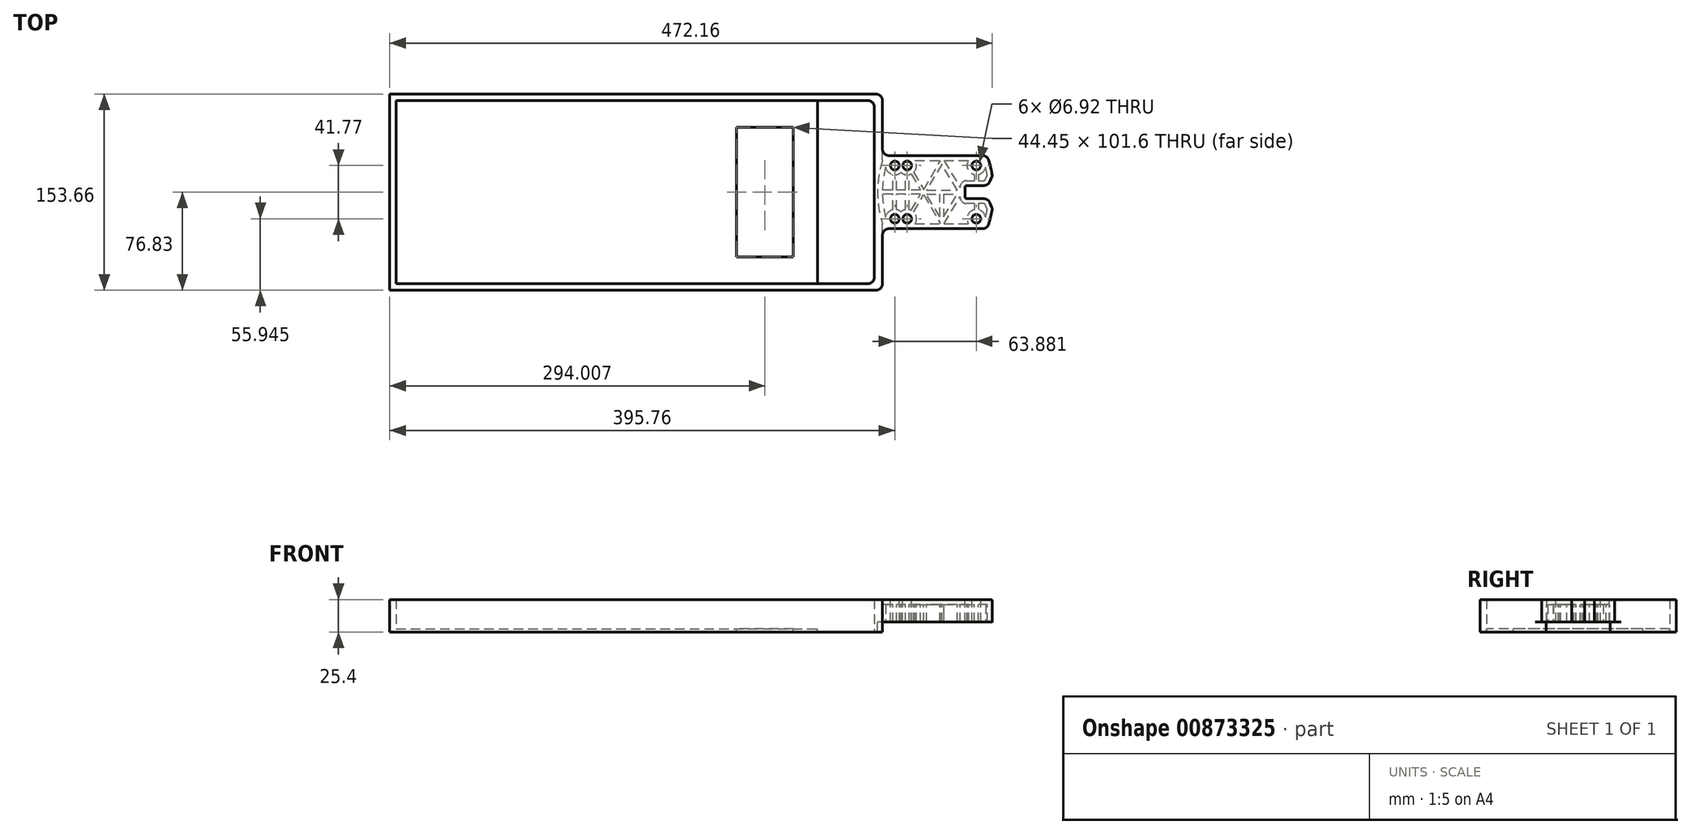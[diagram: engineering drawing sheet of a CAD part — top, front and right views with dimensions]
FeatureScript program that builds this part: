
annotation { "Feature Type Name" : "Feature", "Feature Type Description" : "" }
export const myFeature = defineFeature(function(context is Context, id is Id, definition is map)
    precondition{}
    {
        {
            var Q0;
            Q0=qCreatedBy(makeId("Top.planeOp"),FACE);
            var sketch = newSketch(context, id + "F0", { "sketchPlane" : qUnion([Q0])});
            skPoint(sketch, "E0.middle", {"position": v(0, 0) * mm});
            skLineSegment(sketch, "E1", {"start": v(-45.43, 0) * mm, "end": v(45.43, 0) * mm, "construction": true});
            skLineSegment(sketch, "E2", {"start": v(0, 28.7) * mm, "end": v(0, -28.7) * mm, "construction": true});
            skLineSegment(sketch, "E3", {"start": v(-31.94, 17.42) * mm, "end": v(-31.94, -17.42) * mm, "construction": true});
            skPoint(sketch, "E4", {"position": v(-31.94, 0) * mm});
            skCircle(sketch, "E5", {"center": v(-31.94, 20.89) * mm, "radius": 3.46 * mm});
            skLineSegment(sketch, "E6", {"start": v(-22.22, -17.42) * mm, "end": v(-22.23, 17.42) * mm, "construction": true});
            skPoint(sketch, "E7", {"position": v(-22.23, 0) * mm});
            skCircle(sketch, "E8", {"center": v(-22.23, 20.89) * mm, "radius": 3.46 * mm});
            skLineSegment(sketch, "E9", {"start": v(31.94, 17.42) * mm, "end": v(31.94, -17.42) * mm, "construction": true});
            skPoint(sketch, "E10", {"position": v(31.94, 0) * mm});
            skCircle(sketch, "E11", {"center": v(31.94, 20.89) * mm, "radius": 3.46 * mm});
            skPoint(sketch, "E12", {"position": v(-28.48, 20.89) * mm});
            skPoint(sketch, "E13", {"position": v(-25.69, 20.89) * mm});
            skPoint(sketch, "E14", {"position": v(-18.76, 20.89) * mm});
            skPoint(sketch, "E15", {"position": v(28.48, 20.89) * mm});
            skLineSegment(sketch, "E16", {"start": v(-40.35, 28.7) * mm, "end": v(40.35, 28.7) * mm});
            skPoint(sketch, "E17", {"position": v(0, 28.7) * mm});
            skArc(sketch, "E18", {"start": v(-40.35, 28.7) * mm, "mid": v(-44.15, 14.57) * mm, "end": v(-45.43, 0) * mm});
            skArc(sketch, "E19", {"start": v(45.43, 0) * mm, "mid": v(44.15, 14.57) * mm, "end": v(40.35, 28.7) * mm});
            skLineSegment(sketch, "E20", {"start": v(-31.94, 20.89) * mm, "end": v(31.94, 20.89) * mm, "construction": true});
            skPoint(sketch, "E21", {"position": v(0, 20.89) * mm});
            skArc(sketch, "E22.MirrorCS", {"start": v(-40.35, -28.7) * mm, "mid": v(-44.15, -14.57) * mm, "end": v(-45.43, 0) * mm});
            skLineSegment(sketch, "E23.MirrorCS", {"start": v(-40.35, -28.7) * mm, "end": v(40.35, -28.7) * mm});
            skCircle(sketch, "E24.MirrorC", {"center": v(-31.94, -20.89) * mm, "radius": 3.46 * mm});
            skCircle(sketch, "E25.MirrorC", {"center": v(-22.23, -20.89) * mm, "radius": 3.46 * mm});
            skCircle(sketch, "E26.MirrorC", {"center": v(31.94, -20.89) * mm, "radius": 3.46 * mm});
            skArc(sketch, "E27.MirrorCS", {"start": v(45.43, 0) * mm, "mid": v(44.15, -14.57) * mm, "end": v(40.35, -28.7) * mm});
            skSolve(sketch);
        }
        {
            var Q0;
            Q0=makeQuery(id+"F0.imprint","IMPRINT",FACE,{"disambiguationData":[TD([[makeQuery(id+"F0.imprint","IMPRINT",EDGE,{"derivedFrom":sQuery(id+"F0.wireOp",EDGE,"E5")}),-1.0]])]});
            extrude(context, id + "F1", {"entities" : qUnion([Q0]), "oppositeDirection" : true, "depth" : 17.6 * mm, "offsetDistance" : 25.4 * mm});
        }
        {
            var Q0;
            Q0=makeQuery(id+"F1.opExtrude","CAP_FACE",FACE,{"disambiguationData":[OSD([sQuery(id+"F0.wireOp",EDGE,"E5"),sQuery(id+"F0.wireOp",EDGE,"E8"),sQuery(id+"F0.wireOp",EDGE,"E11"),sQuery(id+"F0.wireOp",EDGE,"E16"),sQuery(id+"F0.wireOp",EDGE,"E18"),sQuery(id+"F0.wireOp",EDGE,"E19"),sQuery(id+"F0.wireOp",EDGE,"E22.MirrorCS"),sQuery(id+"F0.wireOp",EDGE,"E23.MirrorCS"),sQuery(id+"F0.wireOp",EDGE,"E24.MirrorC"),sQuery(id+"F0.wireOp",EDGE,"E25.MirrorC"),sQuery(id+"F0.wireOp",EDGE,"E26.MirrorC"),sQuery(id+"F0.wireOp",EDGE,"E27.MirrorCS")])],"isStart":true});
            var sketch = newSketch(context, id + "F2", { "sketchPlane" : qUnion([Q0])});
            skLineSegment(sketch, "E28", {"start": v(44.46, -12.7) * mm, "end": v(41.19, -5.2) * mm});
            skLineSegment(sketch, "E29", {"start": v(41.19, -5.2) * mm, "end": v(23.15, -5.2) * mm});
            skLineSegment(sketch, "E30", {"start": v(23.15, -5.2) * mm, "end": v(23.15, 5.2) * mm});
            skLineSegment(sketch, "E31", {"start": v(23.15, 5.2) * mm, "end": v(41.19, 5.2) * mm});
            skLineSegment(sketch, "E32", {"start": v(41.19, 5.2) * mm, "end": v(44.46, 12.7) * mm});
            skPoint(sketch, "E33", {"position": v(23.15, 0) * mm});
            skLineSegment(sketch, "E34", {"start": v(44.46, -12.7) * mm, "end": v(44.46, 12.7) * mm, "construction": true});
            skPoint(sketch, "E35", {"position": v(-45.43, 0) * mm});
            skArc(sketch, "E36", {"start": v(44.46, -12.7) * mm, "mid": v(45.43, 0) * mm, "end": v(44.46, 12.7) * mm});
            skSolve(sketch);
        }
        {
            var Q0;
            Q0=makeQuery(id+"F2.imprint","IMPRINT",FACE,{"disambiguationData":[TD([[makeQuery(id+"F2.imprint","IMPRINT",EDGE,{"derivedFrom":sQuery(id+"F2.wireOp",EDGE,"E28")}),-1.0]])]});
            extrude(context, id + "F3", {"entities" : qUnion([Q0]), "operationType" : NewBodyOperationType.REMOVE, "endBound" : BoundingType.THROUGH_ALL, "oppositeDirection" : true, "depth" : 25.4 * mm, "offsetDistance" : 25.4 * mm});
        }
        {
            var Q0;
            Q0=makeQuery(id+"F1.opExtrude","SWEPT_EDGE",EDGE,{"disambiguationData":[OSD([sQuery(id+"F0.wireOp",EDGE,"E23.MirrorCS"),sQuery(id+"F0.wireOp",EDGE,"E27.MirrorCS")])]});
            var Q1;
            Q1=makeQuery(id+"F1.opExtrude","SWEPT_EDGE",EDGE,{"disambiguationData":[OSD([sQuery(id+"F0.wireOp",EDGE,"E22.MirrorCS"),sQuery(id+"F0.wireOp",EDGE,"E23.MirrorCS")])]});
            var Q2;
            Q2=makeQuery(id+"F3.boolean.opBoolean","COPY",EDGE,{"derivedFrom":makeQuery(id+"F3.opExtrude","SWEPT_EDGE",EDGE,{"disambiguationData":[OSD([sQuery(id+"F0.wireOp",EDGE,"E19"),sQuery(id+"F0.wireOp",EDGE,"E27.MirrorCS"),sQuery(id+"F2.wireOp",EDGE,"E28"),sQuery(id+"F2.wireOp",EDGE,"E36")])]})});
            var Q3;
            Q3=makeQuery(id+"F3.boolean.opBoolean","COPY",EDGE,{"derivedFrom":makeQuery(id+"F3.opExtrude","SWEPT_EDGE",EDGE,{"disambiguationData":[OSD([sQuery(id+"F2.wireOp",EDGE,"E31"),sQuery(id+"F2.wireOp",EDGE,"E32")])]})});
            var Q4;
            Q4=makeQuery(id+"F3.boolean.opBoolean","COPY",EDGE,{"derivedFrom":makeQuery(id+"F3.opExtrude","SWEPT_EDGE",EDGE,{"disambiguationData":[OSD([sQuery(id+"F0.wireOp",EDGE,"E19"),sQuery(id+"F0.wireOp",EDGE,"E27.MirrorCS"),sQuery(id+"F2.wireOp",EDGE,"E32"),sQuery(id+"F2.wireOp",EDGE,"E36")])]})});
            var Q5;
            Q5=makeQuery(id+"F1.opExtrude","SWEPT_EDGE",EDGE,{"disambiguationData":[OSD([sQuery(id+"F0.wireOp",EDGE,"E16"),sQuery(id+"F0.wireOp",EDGE,"E19")])]});
            var Q6;
            Q6=makeQuery(id+"F3.boolean.opBoolean","COPY",EDGE,{"derivedFrom":makeQuery(id+"F3.opExtrude","SWEPT_EDGE",EDGE,{"disambiguationData":[OSD([sQuery(id+"F2.wireOp",EDGE,"E28"),sQuery(id+"F2.wireOp",EDGE,"E29")])]})});
            var Q7;
            Q7=makeQuery(id+"F1.opExtrude","SWEPT_EDGE",EDGE,{"disambiguationData":[OSD([sQuery(id+"F0.wireOp",EDGE,"E16"),sQuery(id+"F0.wireOp",EDGE,"E18")])]});
            fillet(context, id + "F4", {"entities" : qUnion([Q0, Q1, Q2, Q3, Q4, Q5, Q6, Q7]), "radius" : 5.08 * mm, "tangentPropagation" : true, "allowEdgeOverflow" : false});
        }
        {
            var Q0;
            Q0=makeQuery(id+"F1.opExtrude","CAP_FACE",FACE,{"disambiguationData":[OSD([sQuery(id+"F0.wireOp",EDGE,"E5"),sQuery(id+"F0.wireOp",EDGE,"E8"),sQuery(id+"F0.wireOp",EDGE,"E11"),sQuery(id+"F0.wireOp",EDGE,"E16"),sQuery(id+"F0.wireOp",EDGE,"E18"),sQuery(id+"F0.wireOp",EDGE,"E19"),sQuery(id+"F0.wireOp",EDGE,"E22.MirrorCS"),sQuery(id+"F0.wireOp",EDGE,"E23.MirrorCS"),sQuery(id+"F0.wireOp",EDGE,"E24.MirrorC"),sQuery(id+"F0.wireOp",EDGE,"E25.MirrorC"),sQuery(id+"F0.wireOp",EDGE,"E26.MirrorC"),sQuery(id+"F0.wireOp",EDGE,"E27.MirrorCS")])],"isStart":false});
            shell(context, id + "F5", {"entities" : qUnion([Q0]), "thickness" : 3.8 * mm});
        }
        {
            var Q0;
            Q0=makeQuery(id+"F3.boolean.opBoolean","COPY",EDGE,{"derivedFrom":makeQuery(id+"F3.opExtrude","SWEPT_EDGE",EDGE,{"disambiguationData":[OSD([sQuery(id+"F2.wireOp",EDGE,"E29"),sQuery(id+"F2.wireOp",EDGE,"E30")])]})});
            var Q1;
            Q1=makeQuery(id+"F3.boolean.opBoolean","COPY",EDGE,{"derivedFrom":makeQuery(id+"F3.opExtrude","SWEPT_EDGE",EDGE,{"disambiguationData":[OSD([sQuery(id+"F2.wireOp",EDGE,"E30"),sQuery(id+"F2.wireOp",EDGE,"E31")])]})});
            fillet(context, id + "F6", {"entities" : qUnion([Q0, Q1]), "radius" : 1.27 * mm, "tangentPropagation" : true, "allowEdgeOverflow" : false});
        }
        {
            var Q0;
            Q0=makeQuery(id+"F5.opShell","OFFSET_EDGE",EDGE,{"disambiguationData":[OSD([sQuery(id+"F2.wireOp",EDGE,"E30"),sQuery(id+"F2.wireOp",EDGE,"E31")])]});
            var Q1;
            Q1=makeQuery(id+"F5.opShell","OFFSET_EDGE",EDGE,{"disambiguationData":[OSD([sQuery(id+"F2.wireOp",EDGE,"E29"),sQuery(id+"F2.wireOp",EDGE,"E30")])]});
            fillet(context, id + "F7", {"entities" : qUnion([Q0, Q1]), "radius" : 5.08 * mm, "tangentPropagation" : true, "allowEdgeOverflow" : false});
        }
        {
            var Q0;
            Q0=makeQuery(id+"F5.opShell","OFFSET_FACE",FACE,{"disambiguationData":[OSD([sQuery(id+"F0.wireOp",EDGE,"E5"),sQuery(id+"F0.wireOp",EDGE,"E8"),sQuery(id+"F0.wireOp",EDGE,"E11"),sQuery(id+"F0.wireOp",EDGE,"E16"),sQuery(id+"F0.wireOp",EDGE,"E18"),sQuery(id+"F0.wireOp",EDGE,"E19"),sQuery(id+"F0.wireOp",EDGE,"E22.MirrorCS"),sQuery(id+"F0.wireOp",EDGE,"E23.MirrorCS"),sQuery(id+"F0.wireOp",EDGE,"E24.MirrorC"),sQuery(id+"F0.wireOp",EDGE,"E25.MirrorC"),sQuery(id+"F0.wireOp",EDGE,"E26.MirrorC"),sQuery(id+"F0.wireOp",EDGE,"E27.MirrorCS")])]});
            var sketch = newSketch(context, id + "F8", { "sketchPlane" : qUnion([Q0])});
            skLineSegment(sketch, "E37", {"start": v(-31.94, 20.89) * mm, "end": v(-31.94, -20.89) * mm, "construction": true});
            skLineSegment(sketch, "E38", {"start": v(-22.23, -20.89) * mm, "end": v(-22.23, 20.89) * mm, "construction": true});
            skLineSegment(sketch, "E39", {"start": v(31.94, -20.89) * mm, "end": v(31.94, 20.89) * mm, "construction": true});
            skLineSegment(sketch, "E40.bottom", {"start": v(-33.44, 13.77) * mm, "end": v(-30.44, 13.77) * mm});
            skLineSegment(sketch, "E40.top", {"start": v(-33.44, -13.77) * mm, "end": v(-30.44, -13.77) * mm});
            skLineSegment(sketch, "E40.left", {"start": v(-33.44, 13.77) * mm, "end": v(-33.44, 1.5) * mm});
            skLineSegment(sketch, "E40.right", {"start": v(-30.44, 13.77) * mm, "end": v(-30.44, 1.5) * mm});
            skPoint(sketch, "E40.middle", {"position": v(-31.94, 0) * mm});
            skLineSegment(sketch, "E41.bottom", {"start": v(-23.73, 13.77) * mm, "end": v(-20.73, 13.77) * mm});
            skLineSegment(sketch, "E41.top", {"start": v(-23.73, -13.77) * mm, "end": v(-20.73, -13.77) * mm});
            skLineSegment(sketch, "E41.left", {"start": v(-23.73, 13.77) * mm, "end": v(-23.73, 1.5) * mm});
            skLineSegment(sketch, "E41.right", {"start": v(-20.73, 13.77) * mm, "end": v(-20.73, 1.5) * mm});
            skPoint(sketch, "E41.middle", {"position": v(-22.23, 0) * mm});
            skLineSegment(sketch, "E42.bottom", {"start": v(33.44, -13.77) * mm, "end": v(30.44, -13.77) * mm});
            skLineSegment(sketch, "E42.top", {"start": v(33.44, -9.02) * mm, "end": v(30.44, -9.02) * mm});
            skLineSegment(sketch, "E42.left", {"start": v(33.44, -13.77) * mm, "end": v(33.44, -9.02) * mm});
            skLineSegment(sketch, "E42.right", {"start": v(30.44, -13.77) * mm, "end": v(30.44, -9.02) * mm});
            skPoint(sketch, "E42.middle", {"position": v(31.94, -11.4) * mm});
            skLineSegment(sketch, "E43.bottom", {"start": v(33.44, 9.02) * mm, "end": v(30.44, 9.02) * mm});
            skLineSegment(sketch, "E43.top", {"start": v(33.44, 13.77) * mm, "end": v(30.44, 13.77) * mm});
            skLineSegment(sketch, "E43.left", {"start": v(33.44, 9.02) * mm, "end": v(33.44, 13.77) * mm});
            skLineSegment(sketch, "E43.right", {"start": v(30.44, 9.02) * mm, "end": v(30.44, 13.77) * mm});
            skPoint(sketch, "E43.middle", {"position": v(31.94, 11.4) * mm});
            skLineSegment(sketch, "E44.right", {"start": v(-45.41, -1.5) * mm, "end": v(-45.41, 1.5) * mm});
            skPoint(sketch, "E44.middle", {"position": v(-13.04, 0) * mm});
            skLineSegment(sketch, "E45", {"start": v(-22.23, 20.89) * mm, "end": v(4.86, -24.9) * mm, "construction": true});
            skLineSegment(sketch, "E46", {"start": v(4.86, -24.9) * mm, "end": v(31.94, 20.89) * mm, "construction": true});
            skLineSegment(sketch, "E47", {"start": v(31.94, -20.89) * mm, "end": v(4.86, 24.9) * mm, "construction": true});
            skLineSegment(sketch, "E48", {"start": v(4.86, 24.9) * mm, "end": v(-22.23, -20.89) * mm, "construction": true});
            skLineSegment(sketch, "E49", {"start": v(-17.31, -15.53) * mm, "end": v(-9.27, -1.93) * mm});
            skLineSegment(sketch, "E50", {"start": v(4.86, 21.95) * mm, "end": v(16.95, 1.5) * mm});
            skLineSegment(sketch, "E51", {"start": v(-19.23, -14.26) * mm, "end": v(-11.69, -1.5) * mm});
            skLineSegment(sketch, "E52", {"start": v(6.6, 24.9) * mm, "end": v(19.34, 3.36) * mm});
            skLineSegment(sketch, "E53", {"start": v(3.93, 24.9) * mm, "end": v(6.6, 24.9) * mm});
            skArc(sketch, "E54", {"start": v(-19.23, -14.26) * mm, "mid": v(-18.22, -14.82) * mm, "end": v(-17.31, -15.53) * mm});
            skLineSegment(sketch, "E55", {"start": v(-51.7, 0) * mm, "end": v(53.56, 0) * mm, "construction": true});
            skLineSegment(sketch, "E56.MirrorCS", {"start": v(-19.23, 14.26) * mm, "end": v(-11.69, 1.5) * mm});
            skLineSegment(sketch, "E57.MirrorCS", {"start": v(-17.31, 15.53) * mm, "end": v(-9.27, 1.93) * mm});
            skLineSegment(sketch, "E58.MirrorCS", {"start": v(4.86, -21.95) * mm, "end": v(16.95, -1.5) * mm});
            skLineSegment(sketch, "E59.MirrorCS", {"start": v(6.6, -24.9) * mm, "end": v(19.34, -3.36) * mm});
            skArc(sketch, "E60.MirrorCS", {"start": v(-19.23, 14.26) * mm, "mid": v(-18.22, 14.82) * mm, "end": v(-17.31, 15.53) * mm});
            skLineSegment(sketch, "E61.trimOffspring", {"start": v(-23.73, -1.5) * mm, "end": v(-23.73, -13.77) * mm});
            skLineSegment(sketch, "E62.trimOffspring", {"start": v(-23.73, 1.5) * mm, "end": v(-30.44, 1.5) * mm});
            skLineSegment(sketch, "E63.trimOffspring", {"start": v(-20.73, -1.5) * mm, "end": v(-20.73, -13.77) * mm});
            skLineSegment(sketch, "E64.trimOffspring", {"start": v(-23.73, -1.5) * mm, "end": v(-30.44, -1.5) * mm});
            skLineSegment(sketch, "E65.trimOffspring", {"start": v(-30.44, -1.5) * mm, "end": v(-30.44, -13.77) * mm});
            skLineSegment(sketch, "E66.trimOffspring", {"start": v(-33.44, 1.5) * mm, "end": v(-45.41, 1.5) * mm});
            skLineSegment(sketch, "E67.trimOffspring", {"start": v(-33.44, -1.5) * mm, "end": v(-33.44, -13.77) * mm});
            skLineSegment(sketch, "E68.trimOffspring", {"start": v(-33.44, -1.5) * mm, "end": v(-45.41, -1.5) * mm});
            skLineSegment(sketch, "E69.trimOffspring", {"start": v(-11.69, -1.5) * mm, "end": v(-20.73, -1.5) * mm});
            skLineSegment(sketch, "E70.trimOffspring", {"start": v(-9.27, -1.93) * mm, "end": v(3.93, -24.9) * mm});
            skLineSegment(sketch, "E71.trimOffspring", {"start": v(-7.24, 1.5) * mm, "end": v(4.86, 21.95) * mm});
            skLineSegment(sketch, "E72.trimOffspring", {"start": v(-7.24, -1.5) * mm, "end": v(4.86, -21.95) * mm});
            skLineSegment(sketch, "E73.trimOffspring", {"start": v(-11.69, 1.5) * mm, "end": v(-20.73, 1.5) * mm});
            skLineSegment(sketch, "E74.trimOffspring", {"start": v(-9.27, 1.93) * mm, "end": v(3.93, 24.9) * mm});
            skLineSegment(sketch, "E75.trimOffspring", {"start": v(16.95, -1.5) * mm, "end": v(-7.24, -1.5) * mm});
            skLineSegment(sketch, "E76.trimOffspring", {"start": v(16.95, 1.5) * mm, "end": v(-7.24, 1.5) * mm});
            skLineSegment(sketch, "E77", {"start": v(19.34, -3.36) * mm, "end": v(19.34, 3.36) * mm});
            skPoint(sketch, "E78", {"position": v(19.34, 0) * mm});
            skSolve(sketch);
        }
        {
            var Q0;
            {var subQ8=sQuery(id+"F8.wireOp",EDGE,"E40.left");Q0=makeQuery(id+"F8.imprint","IMPRINT",FACE,{"disambiguationData":[TD([[makeQuery(id+"F8.imprint","IMPRINT",EDGE,{"derivedFrom":subQ8}),1.0]])]});}
            var Q1;
            Q1=makeQuery(id+"F1.opExtrude","CAP_FACE",FACE,{"disambiguationData":[OSD([sQuery(id+"F0.wireOp",EDGE,"E5"),sQuery(id+"F0.wireOp",EDGE,"E8"),sQuery(id+"F0.wireOp",EDGE,"E11"),sQuery(id+"F0.wireOp",EDGE,"E16"),sQuery(id+"F0.wireOp",EDGE,"E18"),sQuery(id+"F0.wireOp",EDGE,"E19"),sQuery(id+"F0.wireOp",EDGE,"E22.MirrorCS"),sQuery(id+"F0.wireOp",EDGE,"E23.MirrorCS"),sQuery(id+"F0.wireOp",EDGE,"E24.MirrorC"),sQuery(id+"F0.wireOp",EDGE,"E25.MirrorC"),sQuery(id+"F0.wireOp",EDGE,"E26.MirrorC"),sQuery(id+"F0.wireOp",EDGE,"E27.MirrorCS")])],"isStart":false});
            extrude(context, id + "F9", {"entities" : qUnion([Q0]), "operationType" : NewBodyOperationType.ADD, "endBound" : BoundingType.UP_TO_SURFACE, "depth" : 25.4 * mm, "endBoundEntityFace" : qUnion([Q1]), "offsetDistance" : 25.4 * mm});
        }
        {
            var Q0;
            Q0=makeQuery(id+"F8.imprint","IMPRINT",FACE,{"disambiguationData":[TD([[makeQuery(id+"F8.imprint","IMPRINT",EDGE,{"derivedFrom":sQuery(id+"F8.wireOp",EDGE,"E43.bottom")}),-1.0]])]});
            var Q1;
            Q1=makeQuery(id+"F8.imprint","IMPRINT",FACE,{"disambiguationData":[TD([[makeQuery(id+"F8.imprint","IMPRINT",EDGE,{"derivedFrom":sQuery(id+"F8.wireOp",EDGE,"E42.top")}),-1.0]])]});
            var Q2;
            {var subQ0=sQuery(id+"F0.wireOp",EDGE,"E25.MirrorC");var subQ1=sQuery(id+"F0.wireOp",EDGE,"E24.MirrorC");var subQ2=sQuery(id+"F0.wireOp",EDGE,"E22.MirrorCS");var subQ3=sQuery(id+"F0.wireOp",EDGE,"E18");var subQ4=sQuery(id+"F0.wireOp",EDGE,"E16");var subQ5=sQuery(id+"F0.wireOp",EDGE,"E8");var subQ6=sQuery(id+"F0.wireOp",EDGE,"E5");Q2=makeQuery(id+"F9.boolean.opBoolean","MERGE",FACE,{"derivedFrom":[makeQuery(id+"F1.opExtrude","CAP_FACE",FACE,{"disambiguationData":[OSD([subQ6,subQ5,sQuery(id+"F0.wireOp",EDGE,"E11"),subQ4,subQ3,sQuery(id+"F0.wireOp",EDGE,"E19"),subQ2,sQuery(id+"F0.wireOp",EDGE,"E23.MirrorCS"),subQ1,subQ0,sQuery(id+"F0.wireOp",EDGE,"E26.MirrorC"),sQuery(id+"F0.wireOp",EDGE,"E27.MirrorCS")])],"isStart":false}),makeQuery(id+"F9.opExtrude","CAP_FACE",FACE,{"disambiguationData":[OSD([subQ6,subQ5,subQ4,subQ3,subQ2,subQ1,subQ0,sQuery(id+"F8.wireOp",EDGE,"E40.left"),sQuery(id+"F8.wireOp",EDGE,"E40.right"),sQuery(id+"F8.wireOp",EDGE,"E41.left"),sQuery(id+"F8.wireOp",EDGE,"E41.right"),sQuery(id+"F8.wireOp",EDGE,"E49"),sQuery(id+"F8.wireOp",EDGE,"E50"),sQuery(id+"F8.wireOp",EDGE,"E51"),sQuery(id+"F8.wireOp",EDGE,"E52"),sQuery(id+"F8.wireOp",EDGE,"E53"),sQuery(id+"F8.wireOp",EDGE,"E54"),sQuery(id+"F8.wireOp",EDGE,"E56.MirrorCS"),sQuery(id+"F8.wireOp",EDGE,"E57.MirrorCS"),sQuery(id+"F8.wireOp",EDGE,"E58.MirrorCS"),sQuery(id+"F8.wireOp",EDGE,"E59.MirrorCS"),sQuery(id+"F8.wireOp",EDGE,"E60.MirrorCS"),sQuery(id+"F8.wireOp",EDGE,"E61.trimOffspring"),sQuery(id+"F8.wireOp",EDGE,"E62.trimOffspring"),sQuery(id+"F8.wireOp",EDGE,"E63.trimOffspring"),sQuery(id+"F8.wireOp",EDGE,"E64.trimOffspring"),sQuery(id+"F8.wireOp",EDGE,"E65.trimOffspring"),sQuery(id+"F8.wireOp",EDGE,"E66.trimOffspring"),sQuery(id+"F8.wireOp",EDGE,"E67.trimOffspring"),sQuery(id+"F8.wireOp",EDGE,"E68.trimOffspring"),sQuery(id+"F8.wireOp",EDGE,"E69.trimOffspring"),sQuery(id+"F8.wireOp",EDGE,"E70.trimOffspring"),sQuery(id+"F8.wireOp",EDGE,"E71.trimOffspring"),sQuery(id+"F8.wireOp",EDGE,"E72.trimOffspring"),sQuery(id+"F8.wireOp",EDGE,"E73.trimOffspring"),sQuery(id+"F8.wireOp",EDGE,"E74.trimOffspring"),sQuery(id+"F8.wireOp",EDGE,"E75.trimOffspring"),sQuery(id+"F8.wireOp",EDGE,"E76.trimOffspring"),sQuery(id+"F8.wireOp",EDGE,"E77")])],"isStart":false})]});}
            extrude(context, id + "F10", {"entities" : qUnion([Q0, Q1]), "operationType" : NewBodyOperationType.ADD, "endBound" : BoundingType.UP_TO_SURFACE, "depth" : 25.4 * mm, "endBoundEntityFace" : qUnion([Q2]), "offsetDistance" : 25.4 * mm});
        }
        {
            var Q0;
            Q0=makeQuery(id+"F9.boolean.opBoolean","SPLIT",FACE,{"disambiguationData":[TD([makeQuery(id+"F9.opExtrude","SWEPT_FACE",FACE,{"disambiguationData":[OSD([sQuery(id+"F8.wireOp",EDGE,"E58.MirrorCS")])]})])],"derivedFrom":makeQuery(id+"F5.opShell","OFFSET_FACE",FACE,{"disambiguationData":[OSD([sQuery(id+"F0.wireOp",EDGE,"E5"),sQuery(id+"F0.wireOp",EDGE,"E8"),sQuery(id+"F0.wireOp",EDGE,"E11"),sQuery(id+"F0.wireOp",EDGE,"E16"),sQuery(id+"F0.wireOp",EDGE,"E18"),sQuery(id+"F0.wireOp",EDGE,"E19"),sQuery(id+"F0.wireOp",EDGE,"E22.MirrorCS"),sQuery(id+"F0.wireOp",EDGE,"E23.MirrorCS"),sQuery(id+"F0.wireOp",EDGE,"E24.MirrorC"),sQuery(id+"F0.wireOp",EDGE,"E25.MirrorC"),sQuery(id+"F0.wireOp",EDGE,"E26.MirrorC"),sQuery(id+"F0.wireOp",EDGE,"E27.MirrorCS")])]})});
            var sketch = newSketch(context, id + "F11", { "sketchPlane" : qUnion([Q0])});
            skPoint(sketch, "E79", {"position": v(4.86, 0) * mm});
            skLineSegment(sketch, "E80.bottom", {"start": v(6.36, -24.9) * mm, "end": v(3.36, -24.9) * mm});
            skLineSegment(sketch, "E80.top", {"start": v(6.36, 24.9) * mm, "end": v(3.36, 24.9) * mm});
            skLineSegment(sketch, "E80.left", {"start": v(6.36, -24.9) * mm, "end": v(6.36, 24.9) * mm});
            skLineSegment(sketch, "E80.right", {"start": v(3.36, -24.9) * mm, "end": v(3.36, 24.9) * mm});
            skSolve(sketch);
        }
        {
            var Q0;
            {var subQ1=makeQuery(id+"F9.opExtrude","CAP_EDGE",EDGE,{"disambiguationData":[OSD([sQuery(id+"F8.wireOp",EDGE,"E58.MirrorCS")])],"isStart":true});var subQ3=sQuery(id+"F11.wireOp",EDGE,"E80.left");var subQ4=makeQuery(id+"F11.imprint","INTERSECT",VERTEX,{"derivedFrom":[subQ1,subQ3]});Q0=makeQuery(id+"F11.imprint","IMPRINT",FACE,{"disambiguationData":[TD([[makeQuery(id+"F11.imprint","IMPRINT",EDGE,{"disambiguationData":[TD([[subQ4,-1.0]])],"derivedFrom":subQ3}),1.0]])]});}
            var Q1;
            {var subQ0=sQuery(id+"F11.wireOp",EDGE,"E80.top");Q1=makeQuery(id+"F11.imprint","IMPRINT",FACE,{"disambiguationData":[TD([[makeQuery(id+"F11.imprint","IMPRINT",EDGE,{"derivedFrom":subQ0}),1.0]])]});}
            var Q2;
            {var subQ0=sQuery(id+"F0.wireOp",EDGE,"E26.MirrorC");var subQ1=sQuery(id+"F0.wireOp",EDGE,"E11");var subQ2=sQuery(id+"F0.wireOp",EDGE,"E25.MirrorC");var subQ3=sQuery(id+"F0.wireOp",EDGE,"E24.MirrorC");var subQ4=sQuery(id+"F0.wireOp",EDGE,"E22.MirrorCS");var subQ5=sQuery(id+"F0.wireOp",EDGE,"E18");var subQ6=sQuery(id+"F0.wireOp",EDGE,"E16");var subQ7=sQuery(id+"F0.wireOp",EDGE,"E8");var subQ8=sQuery(id+"F0.wireOp",EDGE,"E5");Q2=makeQuery(id+"F10.boolean.opBoolean","MERGE",FACE,{"derivedFrom":[makeQuery(id+"F9.boolean.opBoolean","MERGE",FACE,{"derivedFrom":[makeQuery(id+"F1.opExtrude","CAP_FACE",FACE,{"disambiguationData":[OSD([subQ8,subQ7,subQ1,subQ6,subQ5,sQuery(id+"F0.wireOp",EDGE,"E19"),subQ4,sQuery(id+"F0.wireOp",EDGE,"E23.MirrorCS"),subQ3,subQ2,subQ0,sQuery(id+"F0.wireOp",EDGE,"E27.MirrorCS")])],"isStart":false}),makeQuery(id+"F9.opExtrude","CAP_FACE",FACE,{"disambiguationData":[OSD([subQ8,subQ7,subQ6,subQ5,subQ4,subQ3,subQ2,sQuery(id+"F8.wireOp",EDGE,"E40.left"),sQuery(id+"F8.wireOp",EDGE,"E40.right"),sQuery(id+"F8.wireOp",EDGE,"E41.left"),sQuery(id+"F8.wireOp",EDGE,"E41.right"),sQuery(id+"F8.wireOp",EDGE,"E49"),sQuery(id+"F8.wireOp",EDGE,"E50"),sQuery(id+"F8.wireOp",EDGE,"E51"),sQuery(id+"F8.wireOp",EDGE,"E52"),sQuery(id+"F8.wireOp",EDGE,"E53"),sQuery(id+"F8.wireOp",EDGE,"E54"),sQuery(id+"F8.wireOp",EDGE,"E56.MirrorCS"),sQuery(id+"F8.wireOp",EDGE,"E57.MirrorCS"),sQuery(id+"F8.wireOp",EDGE,"E58.MirrorCS"),sQuery(id+"F8.wireOp",EDGE,"E59.MirrorCS"),sQuery(id+"F8.wireOp",EDGE,"E60.MirrorCS"),sQuery(id+"F8.wireOp",EDGE,"E61.trimOffspring"),sQuery(id+"F8.wireOp",EDGE,"E62.trimOffspring"),sQuery(id+"F8.wireOp",EDGE,"E63.trimOffspring"),sQuery(id+"F8.wireOp",EDGE,"E64.trimOffspring"),sQuery(id+"F8.wireOp",EDGE,"E65.trimOffspring"),sQuery(id+"F8.wireOp",EDGE,"E66.trimOffspring"),sQuery(id+"F8.wireOp",EDGE,"E67.trimOffspring"),sQuery(id+"F8.wireOp",EDGE,"E68.trimOffspring"),sQuery(id+"F8.wireOp",EDGE,"E69.trimOffspring"),sQuery(id+"F8.wireOp",EDGE,"E70.trimOffspring"),sQuery(id+"F8.wireOp",EDGE,"E71.trimOffspring"),sQuery(id+"F8.wireOp",EDGE,"E72.trimOffspring"),sQuery(id+"F8.wireOp",EDGE,"E73.trimOffspring"),sQuery(id+"F8.wireOp",EDGE,"E74.trimOffspring"),sQuery(id+"F8.wireOp",EDGE,"E75.trimOffspring"),sQuery(id+"F8.wireOp",EDGE,"E76.trimOffspring"),sQuery(id+"F8.wireOp",EDGE,"E77")])],"isStart":false})]}),makeQuery(id+"F10.opExtrude","CAP_FACE",FACE,{"disambiguationData":[OSD([subQ1,sQuery(id+"F8.wireOp",EDGE,"E42.top"),sQuery(id+"F8.wireOp",EDGE,"E42.left"),sQuery(id+"F8.wireOp",EDGE,"E42.right")])],"isStart":false}),makeQuery(id+"F10.opExtrude","CAP_FACE",FACE,{"disambiguationData":[OSD([subQ0,sQuery(id+"F8.wireOp",EDGE,"E43.bottom"),sQuery(id+"F8.wireOp",EDGE,"E43.left"),sQuery(id+"F8.wireOp",EDGE,"E43.right")])],"isStart":false})]});}
            extrude(context, id + "F12", {"entities" : qUnion([Q0, Q1]), "operationType" : NewBodyOperationType.ADD, "endBound" : BoundingType.UP_TO_SURFACE, "depth" : 25.4 * mm, "endBoundEntityFace" : qUnion([Q2]), "offsetDistance" : 25.4 * mm});
        }
        {
            var Q0;
            Q0=qCreatedBy(makeId("Top.planeOp"),FACE);
            var sketch = newSketch(context, id + "F13", { "sketchPlane" : qUnion([Q0])});
            skLineSegment(sketch, "E81.bottom", {"start": v(-41.56, -76.83) * mm, "end": v(-427.7, -76.83) * mm});
            skLineSegment(sketch, "E81.top", {"start": v(-41.56, 76.83) * mm, "end": v(-427.7, 76.83) * mm});
            skLineSegment(sketch, "E81.left", {"start": v(-41.56, -76.83) * mm, "end": v(-41.56, -33.55) * mm});
            skLineSegment(sketch, "E81.right", {"start": v(-427.7, -76.83) * mm, "end": v(-427.7, 76.83) * mm});
            skPoint(sketch, "E81.middle", {"position": v(-234.63, 0) * mm});
            skArc(sketch, "E82", {"start": v(-36.71, -28.7) * mm, "mid": v(-40.14, -30.12) * mm, "end": v(-41.56, -33.55) * mm});
            skArc(sketch, "E83", {"start": v(-41.56, 33.55) * mm, "mid": v(-40.14, 30.12) * mm, "end": v(-36.71, 28.7) * mm});
            skLineSegment(sketch, "E84.trimOffspring", {"start": v(-41.56, 33.55) * mm, "end": v(-41.56, 76.83) * mm});
            skArc(sketch, "E85.0", {"start": v(-41.56, 25.15) * mm, "mid": v(-39.72, 27.72) * mm, "end": v(-36.71, 28.7) * mm});
            skArc(sketch, "E86.0", {"start": v(-41.56, 25.15) * mm, "mid": v(-45.43, 0) * mm, "end": v(-41.56, -25.15) * mm});
            skArc(sketch, "E87.0", {"start": v(-36.71, -28.7) * mm, "mid": v(-39.72, -27.72) * mm, "end": v(-41.56, -25.15) * mm});
            skLineSegment(sketch, "E88.bottom", {"start": v(-422.62, -71.75) * mm, "end": v(-47.97, -71.75) * mm, "construction": true});
            skLineSegment(sketch, "E88.top", {"start": v(-422.62, 71.76) * mm, "end": v(-47.97, 71.76) * mm, "construction": true});
            skLineSegment(sketch, "E88.left", {"start": v(-422.62, -71.75) * mm, "end": v(-422.62, 71.76) * mm, "construction": true});
            skLineSegment(sketch, "E88.right", {"start": v(-47.97, -71.75) * mm, "end": v(-47.97, 71.76) * mm, "construction": true});
            skPoint(sketch, "E88.middle", {"position": v(-235.3, 0) * mm});
            skLineSegment(sketch, "E89", {"start": v(-92.42, -71.75) * mm, "end": v(-92.42, 71.76) * mm, "construction": true});
            skPoint(sketch, "E90", {"position": v(-45.43, 0) * mm});
            skSolve(sketch);
        }
        {
            var Q0;
            Q0=makeQuery(id+"F13.imprint","IMPRINT",FACE,{"disambiguationData":[TD([[makeQuery(id+"F13.imprint","IMPRINT",EDGE,{"derivedFrom":sQuery(id+"F13.wireOp",EDGE,"E81.bottom")}),-1.0]])]});
            extrude(context, id + "F14", {"entities" : qUnion([Q0]), "oppositeDirection" : true, "depth" : 25.4 * mm, "offsetDistance" : 25.4 * mm});
        }
        {
            var Q0;
            Q0=makeQuery(id+"F14.opExtrude","SWEPT_BODY",BODY,{"disambiguationData":[OSD([sQuery(id+"F13.wireOp",EDGE,"E81.bottom"),sQuery(id+"F13.wireOp",EDGE,"E81.top"),sQuery(id+"F13.wireOp",EDGE,"E81.left"),sQuery(id+"F13.wireOp",EDGE,"E81.right"),sQuery(id+"F13.wireOp",EDGE,"E82"),sQuery(id+"F13.wireOp",EDGE,"E83"),sQuery(id+"F13.wireOp",EDGE,"E84.trimOffspring"),sQuery(id+"F13.wireOp",EDGE,"E85.0"),sQuery(id+"F13.wireOp",EDGE,"E86.0"),sQuery(id+"F13.wireOp",EDGE,"E87.0")])]});
            var Q1;
            Q1=makeQuery(id+"F1.opExtrude","SWEPT_BODY",BODY,{"disambiguationData":[OSD([sQuery(id+"F0.wireOp",EDGE,"E5"),sQuery(id+"F0.wireOp",EDGE,"E8"),sQuery(id+"F0.wireOp",EDGE,"E11"),sQuery(id+"F0.wireOp",EDGE,"E16"),sQuery(id+"F0.wireOp",EDGE,"E18"),sQuery(id+"F0.wireOp",EDGE,"E19"),sQuery(id+"F0.wireOp",EDGE,"E22.MirrorCS"),sQuery(id+"F0.wireOp",EDGE,"E23.MirrorCS"),sQuery(id+"F0.wireOp",EDGE,"E24.MirrorC"),sQuery(id+"F0.wireOp",EDGE,"E25.MirrorC"),sQuery(id+"F0.wireOp",EDGE,"E26.MirrorC"),sQuery(id+"F0.wireOp",EDGE,"E27.MirrorCS")])]});
            booleanBodies(context, id + "F15", {"operationType" : BooleanOperationType.UNION, "tools" : qUnion([Q0, Q1])});
        }
        {
            var Q0;
            {var subQ0=sQuery(id+"F8.wireOp",EDGE,"E72.trimOffspring");var subQ1=sQuery(id+"F8.wireOp",EDGE,"E58.MirrorCS");var subQ2=sQuery(id+"F0.wireOp",EDGE,"E26.MirrorC");var subQ3=sQuery(id+"F0.wireOp",EDGE,"E11");var subQ4=sQuery(id+"F0.wireOp",EDGE,"E25.MirrorC");var subQ5=sQuery(id+"F0.wireOp",EDGE,"E24.MirrorC");var subQ6=sQuery(id+"F0.wireOp",EDGE,"E22.MirrorCS");var subQ7=sQuery(id+"F0.wireOp",EDGE,"E18");var subQ8=sQuery(id+"F0.wireOp",EDGE,"E16");var subQ9=sQuery(id+"F0.wireOp",EDGE,"E8");var subQ10=sQuery(id+"F0.wireOp",EDGE,"E5");Q0=makeQuery(id+"F12.boolean.opBoolean","MERGE",FACE,{"derivedFrom":[makeQuery(id+"F10.boolean.opBoolean","MERGE",FACE,{"derivedFrom":[makeQuery(id+"F9.boolean.opBoolean","MERGE",FACE,{"derivedFrom":[makeQuery(id+"F1.opExtrude","CAP_FACE",FACE,{"disambiguationData":[OSD([subQ10,subQ9,subQ3,subQ8,subQ7,sQuery(id+"F0.wireOp",EDGE,"E19"),subQ6,sQuery(id+"F0.wireOp",EDGE,"E23.MirrorCS"),subQ5,subQ4,subQ2,sQuery(id+"F0.wireOp",EDGE,"E27.MirrorCS")])],"isStart":false}),makeQuery(id+"F9.opExtrude","CAP_FACE",FACE,{"disambiguationData":[OSD([subQ10,subQ9,subQ8,subQ7,subQ6,subQ5,subQ4,sQuery(id+"F8.wireOp",EDGE,"E40.left"),sQuery(id+"F8.wireOp",EDGE,"E40.right"),sQuery(id+"F8.wireOp",EDGE,"E41.left"),sQuery(id+"F8.wireOp",EDGE,"E41.right"),sQuery(id+"F8.wireOp",EDGE,"E49"),sQuery(id+"F8.wireOp",EDGE,"E50"),sQuery(id+"F8.wireOp",EDGE,"E51"),sQuery(id+"F8.wireOp",EDGE,"E52"),sQuery(id+"F8.wireOp",EDGE,"E53"),sQuery(id+"F8.wireOp",EDGE,"E54"),sQuery(id+"F8.wireOp",EDGE,"E56.MirrorCS"),sQuery(id+"F8.wireOp",EDGE,"E57.MirrorCS"),subQ1,sQuery(id+"F8.wireOp",EDGE,"E59.MirrorCS"),sQuery(id+"F8.wireOp",EDGE,"E60.MirrorCS"),sQuery(id+"F8.wireOp",EDGE,"E61.trimOffspring"),sQuery(id+"F8.wireOp",EDGE,"E62.trimOffspring"),sQuery(id+"F8.wireOp",EDGE,"E63.trimOffspring"),sQuery(id+"F8.wireOp",EDGE,"E64.trimOffspring"),sQuery(id+"F8.wireOp",EDGE,"E65.trimOffspring"),sQuery(id+"F8.wireOp",EDGE,"E66.trimOffspring"),sQuery(id+"F8.wireOp",EDGE,"E67.trimOffspring"),sQuery(id+"F8.wireOp",EDGE,"E68.trimOffspring"),sQuery(id+"F8.wireOp",EDGE,"E69.trimOffspring"),sQuery(id+"F8.wireOp",EDGE,"E70.trimOffspring"),sQuery(id+"F8.wireOp",EDGE,"E71.trimOffspring"),subQ0,sQuery(id+"F8.wireOp",EDGE,"E73.trimOffspring"),sQuery(id+"F8.wireOp",EDGE,"E74.trimOffspring"),sQuery(id+"F8.wireOp",EDGE,"E75.trimOffspring"),sQuery(id+"F8.wireOp",EDGE,"E76.trimOffspring"),sQuery(id+"F8.wireOp",EDGE,"E77")])],"isStart":false})]}),makeQuery(id+"F10.opExtrude","CAP_FACE",FACE,{"disambiguationData":[OSD([subQ3,sQuery(id+"F8.wireOp",EDGE,"E42.top"),sQuery(id+"F8.wireOp",EDGE,"E42.left"),sQuery(id+"F8.wireOp",EDGE,"E42.right")])],"isStart":false}),makeQuery(id+"F10.opExtrude","CAP_FACE",FACE,{"disambiguationData":[OSD([subQ2,sQuery(id+"F8.wireOp",EDGE,"E43.bottom"),sQuery(id+"F8.wireOp",EDGE,"E43.left"),sQuery(id+"F8.wireOp",EDGE,"E43.right")])],"isStart":false})]}),makeQuery(id+"F12.opExtrude","CAP_FACE",FACE,{"disambiguationData":[OSD([subQ1,subQ0,sQuery(id+"F11.wireOp",EDGE,"E80.top"),sQuery(id+"F11.wireOp",EDGE,"E80.left"),sQuery(id+"F11.wireOp",EDGE,"E80.right")])],"isStart":false})]});}
            var sketch = newSketch(context, id + "F16", { "sketchPlane" : qUnion([Q0])});
            skLineSegment(sketch, "E91.bottom", {"start": v(-41.56, 33.55) * mm, "end": v(38.2, 33.55) * mm});
            skLineSegment(sketch, "E91.top", {"start": v(-41.56, -33.55) * mm, "end": v(38.2, -33.55) * mm});
            skLineSegment(sketch, "E91.left", {"start": v(-41.56, 33.55) * mm, "end": v(-41.56, -33.55) * mm});
            skLineSegment(sketch, "E91.right", {"start": v(38.2, 33.55) * mm, "end": v(38.2, -33.55) * mm});
            skSolve(sketch);
        }
        {
            var Q0;
            {var subQ3=sQuery(id+"F16.wireOp",EDGE,"E91.top");Q0=makeQuery(id+"F16.imprint","IMPRINT",FACE,{"disambiguationData":[TD([[makeQuery(id+"F16.imprint","IMPRINT",EDGE,{"derivedFrom":subQ3}),1.0]])]});}
            var Q1;
            {var subQ1=sQuery(id+"F16.wireOp",EDGE,"E91.bottom");Q1=makeQuery(id+"F16.imprint","IMPRINT",FACE,{"disambiguationData":[TD([[makeQuery(id+"F16.imprint","IMPRINT",EDGE,{"derivedFrom":subQ1}),-1.0]])]});}
            extrude(context, id + "F17", {"entities" : qUnion([Q0, Q1]), "operationType" : NewBodyOperationType.REMOVE, "depth" : 25.4 * mm, "offsetDistance" : 25.4 * mm});
        }
        {
            var Q0;
            Q0=makeQuery(id+"F14.opExtrude","CAP_FACE",FACE,{"disambiguationData":[OSD([sQuery(id+"F13.wireOp",EDGE,"E81.bottom"),sQuery(id+"F13.wireOp",EDGE,"E81.top"),sQuery(id+"F13.wireOp",EDGE,"E81.left"),sQuery(id+"F13.wireOp",EDGE,"E81.right"),sQuery(id+"F13.wireOp",EDGE,"E82"),sQuery(id+"F13.wireOp",EDGE,"E83"),sQuery(id+"F13.wireOp",EDGE,"E84.trimOffspring"),sQuery(id+"F13.wireOp",EDGE,"E85.0"),sQuery(id+"F13.wireOp",EDGE,"E86.0"),sQuery(id+"F13.wireOp",EDGE,"E87.0")])],"isStart":false});
            var sketch = newSketch(context, id + "F18", { "sketchPlane" : qUnion([Q0])});
            skLineSegment(sketch, "E92.bottom", {"start": v(-422.62, 71.75) * mm, "end": v(-47.97, 71.75) * mm});
            skLineSegment(sketch, "E92.top", {"start": v(-422.62, -71.76) * mm, "end": v(-47.97, -71.76) * mm});
            skLineSegment(sketch, "E92.left", {"start": v(-422.62, 71.75) * mm, "end": v(-422.62, -71.76) * mm});
            skLineSegment(sketch, "E92.right", {"start": v(-47.97, 71.75) * mm, "end": v(-47.97, -71.76) * mm});
            skSolve(sketch);
        }
        {
            var Q0;
            Q0=makeQuery(id+"F18.imprint","IMPRINT",FACE,{"disambiguationData":[TD([[makeQuery(id+"F18.imprint","IMPRINT",EDGE,{"derivedFrom":sQuery(id+"F18.wireOp",EDGE,"E92.bottom")}),-1.0]])]});
            extrude(context, id + "F19", {"entities" : qUnion([Q0]), "operationType" : NewBodyOperationType.REMOVE, "endBound" : BoundingType.THROUGH_ALL, "oppositeDirection" : true, "depth" : 25.4 * mm, "offsetDistance" : 25.4 * mm, "hasSecondDirection" : true, "secondDirectionOppositeDirection" : false, "secondDirectionDepth" : -2.54 * mm});
        }
        {
            var Q0;
            Q0=makeQuery(id+"F13.imprint","IMPRINT",FACE,{"disambiguationData":[TD([[makeQuery(id+"F13.imprint","IMPRINT",EDGE,{"derivedFrom":sQuery(id+"F13.wireOp",EDGE,"E81.bottom")}),-1.0]])]});
            var sketch = newSketch(context, id + "F20", { "sketchPlane" : qUnion([Q0])});
            skLineSegment(sketch, "E93.bottom", {"start": v(-92.42, -71.75) * mm, "end": v(-47.97, -71.75) * mm});
            skLineSegment(sketch, "E93.top", {"start": v(-92.42, 71.76) * mm, "end": v(-47.97, 71.76) * mm});
            skLineSegment(sketch, "E93.left", {"start": v(-92.42, -71.75) * mm, "end": v(-92.42, 71.76) * mm});
            skLineSegment(sketch, "E93.right", {"start": v(-47.97, -71.75) * mm, "end": v(-47.97, 71.76) * mm});
            skSolve(sketch);
        }
        {
            var Q0;
            Q0=makeQuery(id+"F20.imprint","IMPRINT",FACE,{"disambiguationData":[TD([[makeQuery(id+"F20.imprint","IMPRINT",EDGE,{"derivedFrom":sQuery(id+"F20.wireOp",EDGE,"E93.bottom")}),1.0]])]});
            extrude(context, id + "F21", {"entities" : qUnion([Q0]), "operationType" : NewBodyOperationType.REMOVE, "endBound" : BoundingType.THROUGH_ALL, "oppositeDirection" : true, "depth" : 25.4 * mm, "offsetDistance" : 25.4 * mm});
        }
        {
            var Q0;
            Q0=makeQuery(id+"F19.boolean.opBoolean","COPY",FACE,{"derivedFrom":makeQuery(id+"F19.opExtrude","CAP_FACE",FACE,{"disambiguationData":[OSD([sQuery(id+"F18.wireOp",EDGE,"E92.bottom"),sQuery(id+"F18.wireOp",EDGE,"E92.top"),sQuery(id+"F18.wireOp",EDGE,"E92.left"),sQuery(id+"F18.wireOp",EDGE,"E92.right")])],"isStart":true})});
            var sketch = newSketch(context, id + "F22", { "sketchPlane" : qUnion([Q0])});
            skLineSegment(sketch, "E94.bottom", {"start": v(-111.47, 50.8) * mm, "end": v(-155.92, 50.8) * mm});
            skLineSegment(sketch, "E94.top", {"start": v(-111.47, -50.8) * mm, "end": v(-155.92, -50.8) * mm});
            skLineSegment(sketch, "E94.left", {"start": v(-111.47, 50.8) * mm, "end": v(-111.47, -50.8) * mm});
            skLineSegment(sketch, "E94.right", {"start": v(-155.92, 50.8) * mm, "end": v(-155.92, -50.8) * mm});
            skPoint(sketch, "E94.middle", {"position": v(-133.7, 0) * mm});
            skSolve(sketch);
        }
        {
            var Q0;
            Q0=makeQuery(id+"F22.imprint","IMPRINT",FACE,{"disambiguationData":[TD([[makeQuery(id+"F22.imprint","IMPRINT",EDGE,{"derivedFrom":sQuery(id+"F22.wireOp",EDGE,"E94.bottom")}),1.0]])]});
            extrude(context, id + "F23", {"entities" : qUnion([Q0]), "operationType" : NewBodyOperationType.REMOVE, "endBound" : BoundingType.THROUGH_ALL, "oppositeDirection" : true, "depth" : 25.4 * mm, "offsetDistance" : 25.4 * mm});
        }
        {
            var Q0;
            Q0=makeQuery(id+"F14.opExtrude","SWEPT_EDGE",EDGE,{"disambiguationData":[OSD([sQuery(id+"F13.wireOp",EDGE,"E81.bottom"),sQuery(id+"F13.wireOp",EDGE,"E81.left")])]});
            var Q1;
            Q1=makeQuery(id+"F14.opExtrude","SWEPT_EDGE",EDGE,{"disambiguationData":[OSD([sQuery(id+"F13.wireOp",EDGE,"E81.top"),sQuery(id+"F13.wireOp",EDGE,"E84.trimOffspring")])]});
            var Q2;
            Q2=makeQuery(id+"F21.boolean.opBoolean","MERGE",EDGE,{"derivedFrom":[makeQuery(id+"F19.boolean.opBoolean","COPY",EDGE,{"derivedFrom":makeQuery(id+"F19.opExtrude","SWEPT_EDGE",EDGE,{"disambiguationData":[OSD([sQuery(id+"F18.wireOp",EDGE,"E92.top"),sQuery(id+"F18.wireOp",EDGE,"E92.right")])]})})],"fromTools":[makeQuery(id+"F21.opExtrude","SWEPT_EDGE",EDGE,{"disambiguationData":[OSD([sQuery(id+"F20.wireOp",EDGE,"E93.top"),sQuery(id+"F20.wireOp",EDGE,"E93.right")])]})]});
            var Q3;
            Q3=makeQuery(id+"F21.boolean.opBoolean","MERGE",EDGE,{"derivedFrom":[makeQuery(id+"F19.boolean.opBoolean","COPY",EDGE,{"derivedFrom":makeQuery(id+"F19.opExtrude","SWEPT_EDGE",EDGE,{"disambiguationData":[OSD([sQuery(id+"F18.wireOp",EDGE,"E92.bottom"),sQuery(id+"F18.wireOp",EDGE,"E92.right")])]})})],"fromTools":[makeQuery(id+"F21.opExtrude","SWEPT_EDGE",EDGE,{"disambiguationData":[OSD([sQuery(id+"F20.wireOp",EDGE,"E93.bottom"),sQuery(id+"F20.wireOp",EDGE,"E93.right")])]})]});
            fillet(context, id + "F24", {"entities" : qUnion([Q0, Q1, Q2, Q3]), "tangentPropagation" : true, "radius" : 5.08 * mm, "defaultsChanged" : false, "vertexSettings" : [], "allowEdgeOverflow" : false});
        }
    });
